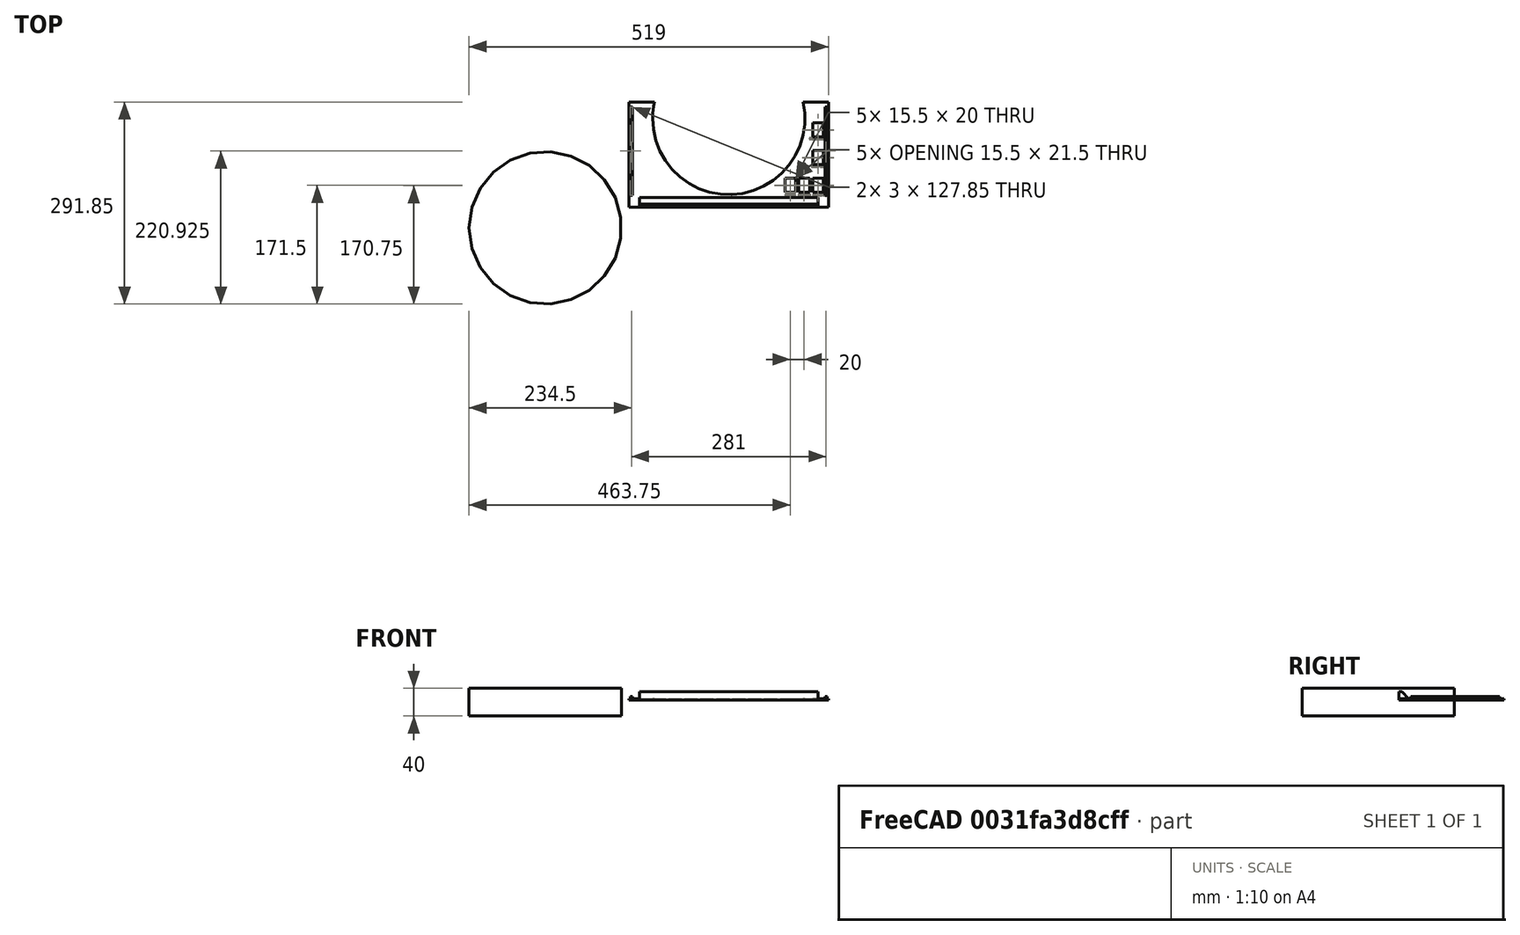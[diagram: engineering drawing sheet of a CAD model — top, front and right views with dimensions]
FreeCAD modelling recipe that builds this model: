
FCSTD DOCUMENT  (FreeCAD 0.17R13522 (Git))
Label: pared_fondo
License: CreativeCommons Attribution-ShareAlike
LicenseURL: http://creativecommons.org/licenses/by-sa/4.0/
objects: Part::Box×13, Part::Cut×12, Part::Extrusion×7, Part::Part2DObjectPython×6, Part::Feature×3, Part::Fuse×3, Part::MultiFuse×1
note: 45 computed .brp shape members not serialized (recipe doc carries the construction recipe); baked Part::Feature solids carry a one-line shape summary decoded from their .brp

FEATURE [Part::Feature] Fusion002002005001001  label="apoyo superior002"
  Placement = pos=(-425,134.85,-44) rot=(1,0,0;3.14159rad)
  shape: bbox 689 x 14 x 10 mm, 7 faces (baked)
FEATURE [Part::Box] Box001  label="Cube001"
  AttacherType = Attacher::AttachEngine3D
  Height = 30
  Length = 500
  Placement = pos=(-485,0,2) rot=(0,0,1;0rad)
  Width = 30
FEATURE [Part::Cut] Cut
  Base = -> Fusion002002005001001
  Refine = true
  Tool = -> Box001
FEATURE [Part::Box] Box  label="Cube"
  AttacherType = Attacher::AttachEngine3D
  Height = 2
  Length = 288
  Width = 151.85
FEATURE [Part::Fuse] Fusion
  Base = -> Box
  Refine = true
  Tool = -> Cut
FEATURE [Part::Part2DObjectPython] Ellipse  # Draft 2D object (typed FeaturePython)
  FirstAngle = 0
  LastAngle = 0
  MajorRadius = 110
  MakeFace = true
  MinorRadius = 110
  Placement = pos=(144,-10,0) rot=(0,1,0;3.14159rad)
FEATURE [Part::Extrusion] Extrude
  Base = -> Ellipse
  Dir = (0,0,-1)
  DirMode = 2
  FaceMakerClass = Part::FaceMakerBullseye
  LengthFwd = 40
  LengthRev = 0
  Placement = pos=(0,138,22) rot=(0,0,1;0rad)
  Solid = false
  Symmetric = false
FEATURE [Part::Extrusion] Extrude001
  Base = -> Ellipse
  Dir = (0,0,-1)
  DirMode = 2
  FaceMakerClass = Part::FaceMakerBullseye
  LengthFwd = 40
  LengthRev = 0
  Placement = pos=(0,0,17) rot=(0,0,1;0rad)
  Solid = false
  Symmetric = false
FEATURE [Part::Cut] Cut001  label="la pared sin apoyos laterales"
  Base = -> Fusion
  Refine = true
  Tool = -> Extrude
FEATURE [Part::Box] Box002  label="lateral derecho"
  AttacherType = Attacher::AttachEngine3D
  Height = 3
  Length = 3
  Placement = pos=(2,17,2) rot=(0,0,1;0rad)
  Width = 127.85
FEATURE [Part::Feature] Box002001  label="lateral izquierda"
  Placement = pos=(283,17,2) rot=(0,0,1;0rad)
  shape: bbox 3 x 127.9 x 3 mm, 6 faces (baked)
FEATURE [Part::Fuse] Fusion002002005001002
  Base = -> Cut001
  Refine = true
  Tool = -> Box002
FEATURE [Part::Fuse] Fusion002002005001003
  Base = -> Box002001
  Refine = true
  Tool = -> Fusion002002005001002
FEATURE [Part::Box] Box002002  label="Cube002"
  AttacherType = Attacher::AttachEngine3D
  Height = 20
  Length = 15.5
  Placement = pos=(225,20,-4) rot=(0,0,1;0rad)
  Width = 21.5
FEATURE [Part::Box] Box002003  label="Cube003"
  AttacherType = Attacher::AttachEngine3D
  Height = 20
  Length = 15.5
  Placement = pos=(245,20,-4) rot=(0,0,1;0rad)
  Width = 21.5
FEATURE [Part::Box] Box002004  label="Cube004"
  AttacherType = Attacher::AttachEngine3D
  Height = 20
  Length = 15.5
  Placement = pos=(265,20,-4) rot=(0,0,1;0rad)
  Width = 21.5
FEATURE [Part::Box] Box002005  label="Cube005"
  AttacherType = Attacher::AttachEngine3D
  Height = 20
  Length = 15.5
  Placement = pos=(265,60,-4) rot=(0,0,1;0rad)
  Width = 21.5
FEATURE [Part::Box] Box002006  label="Cube006"
  AttacherType = Attacher::AttachEngine3D
  Height = 20
  Length = 15.5
  Placement = pos=(265,100,-4) rot=(0,0,1;0rad)
  Width = 21.5
FEATURE [Part::Cut] Cut002
  Base = -> Fusion002002005001003
  Tool = -> Box002004
FEATURE [Part::Cut] Cut003
  Base = -> Cut002
  Tool = -> Box002003
FEATURE [Part::Cut] Cut004
  Base = -> Cut003
  Tool = -> Box002002
FEATURE [Part::Cut] Cut005
  Base = -> Cut004
  Tool = -> Box002006
FEATURE [Part::Cut] Cut006  label="panel fondo con cat5"
  Base = -> Cut005
  Placement = pos=(265,20,0) rot=(0,0,1;0rad)
  Tool = -> Box002005
FEATURE [Part::Box] Box002007  label="Cube007"
  AttacherType = Attacher::AttachEngine3D
  Height = 2
  Length = 15.5
  Placement = pos=(490,40,0) rot=(0,0,1;0rad)
  Width = 1.5
FEATURE [Part::Box] Box002008  label="Cube008"
  AttacherType = Attacher::AttachEngine3D
  Height = 2
  Length = 15.5
  Placement = pos=(510,40,0) rot=(0,0,1;0rad)
  Width = 1.5
FEATURE [Part::Box] Box002009  label="Cube009"
  AttacherType = Attacher::AttachEngine3D
  Height = 2
  Length = 15.5
  Placement = pos=(530,40,0) rot=(0,0,1;0rad)
  Width = 1.5
FEATURE [Part::Box] Box002010  label="Cube010"
  AttacherType = Attacher::AttachEngine3D
  Height = 2
  Length = 15.5
  Placement = pos=(530,80,0) rot=(0,0,1;0rad)
  Width = 1.5
FEATURE [Part::Box] Box002011  label="Cube011"
  AttacherType = Attacher::AttachEngine3D
  Height = 2
  Length = 15.5
  Placement = pos=(530,120,0) rot=(0,0,1;0rad)
  Width = 1.5
FEATURE [Part::MultiFuse] Fusion002002005001004
  Shapes = -> [Cut006,Box002007,Box002008,Box002009,Box002010,Box002011]
FEATURE [Part::Feature] Fusion002002005001004001  label="Fusion002002005001005"
  shape: bbox 288 x 151.9 x 12 mm, 44 faces (baked)
FEATURE [Part::Part2DObjectPython] ShapeString  label="ext-1-8"  # Draft 2D object (typed FeaturePython)
  FontFile = C:/Program Files/FreeCAD 0.17/SigmarOne-Regular.ttf
  Placement = pos=(489.8,38.1871,0) rot=(1,0,0;3.14159rad)
  Size = 2
  String = Ext 1-8
  Tracking = 0
FEATURE [Part::Part2DObjectPython] ShapeString001  label="ext-t9-16"  # Draft 2D object (typed FeaturePython)
  FontFile = C:/Program Files/FreeCAD 0.17/SigmarOne-Regular.ttf
  Placement = pos=(509.244,38.2288,0) rot=(1,0,0;3.14159rad)
  Size = 2
  String = Ext 9-16
  Tracking = 0
FEATURE [Part::Part2DObjectPython] ShapeString002  label="ext-17-24"  # Draft 2D object (typed FeaturePython)
  FontFile = C:/Program Files/FreeCAD 0.17/SigmarOne-Regular.ttf
  Placement = pos=(530.119,38.3714,0) rot=(1,0,0;3.14159rad)
  Size = 2
  String = Ext 17-24
  Tracking = 0
FEATURE [Part::Part2DObjectPython] ShapeString003  label="address bus"  # Draft 2D object (typed FeaturePython)
  FontFile = C:/Program Files/FreeCAD 0.17/SigmarOne-Regular.ttf
  Placement = pos=(527.802,79.9389,0) rot=(1,0,0;3.14159rad)
  Size = 2
  String = addr.bus
  Tracking = 0
FEATURE [Part::Part2DObjectPython] ShapeString004  label="output bus"  # Draft 2D object (typed FeaturePython)
  FontFile = C:/Program Files/FreeCAD 0.17/SigmarOne-Regular.ttf
  Placement = pos=(525.061,119.939,0) rot=(1,0,0;3.14159rad)
  Size = 2
  String = output TLD
  Tracking = 0
FEATURE [Part::Extrusion] Extrude002
  Base = -> ShapeString004
  Dir = (0,0,-1)
  DirMode = 2
  FaceMakerClass = Part::FaceMakerBullseye
  LengthFwd = 1
  LengthRev = 0
  Placement = pos=(0,0,1) rot=(0,0,1;0rad)
  Solid = false
  Symmetric = false
FEATURE [Part::Extrusion] Extrude003
  Base = -> ShapeString003
  Dir = (0,0,-1)
  DirMode = 2
  FaceMakerClass = Part::FaceMakerBullseye
  LengthFwd = 1
  LengthRev = 0
  Placement = pos=(0,0,1) rot=(0,0,1;0rad)
  Solid = false
  Symmetric = false
FEATURE [Part::Extrusion] Extrude004
  Base = -> ShapeString002
  Dir = (0,0,-1)
  DirMode = 2
  FaceMakerClass = Part::FaceMakerBullseye
  LengthFwd = 1
  LengthRev = 0
  Placement = pos=(0,0,1) rot=(0,0,1;0rad)
  Solid = false
  Symmetric = false
FEATURE [Part::Extrusion] Extrude005
  Base = -> ShapeString001
  Dir = (0,0,-1)
  DirMode = 2
  FaceMakerClass = Part::FaceMakerBullseye
  LengthFwd = 1
  LengthRev = 0
  Placement = pos=(0,0,1) rot=(0,0,1;0rad)
  Solid = false
  Symmetric = false
FEATURE [Part::Extrusion] Extrude006
  Base = -> ShapeString
  Dir = (0,0,-1)
  DirMode = 2
  FaceMakerClass = Part::FaceMakerBullseye
  LengthFwd = 1
  LengthRev = 0
  Placement = pos=(0,0,1) rot=(0,0,1;0rad)
  Solid = false
  Symmetric = false
FEATURE [Part::Cut] Cut007
  Base = -> Fusion002002005001004001
  Tool = -> Extrude002
FEATURE [Part::Cut] Cut008
  Base = -> Cut007
  Tool = -> Extrude003
FEATURE [Part::Cut] Cut009
  Base = -> Cut008
  Tool = -> Extrude004
FEATURE [Part::Cut] Cut010
  Base = -> Cut009
  Tool = -> Extrude006
FEATURE [Part::Cut] Cut011  label="panel con cat5 y letras caladas"
  Base = -> Cut010
  Tool = -> Extrude005
